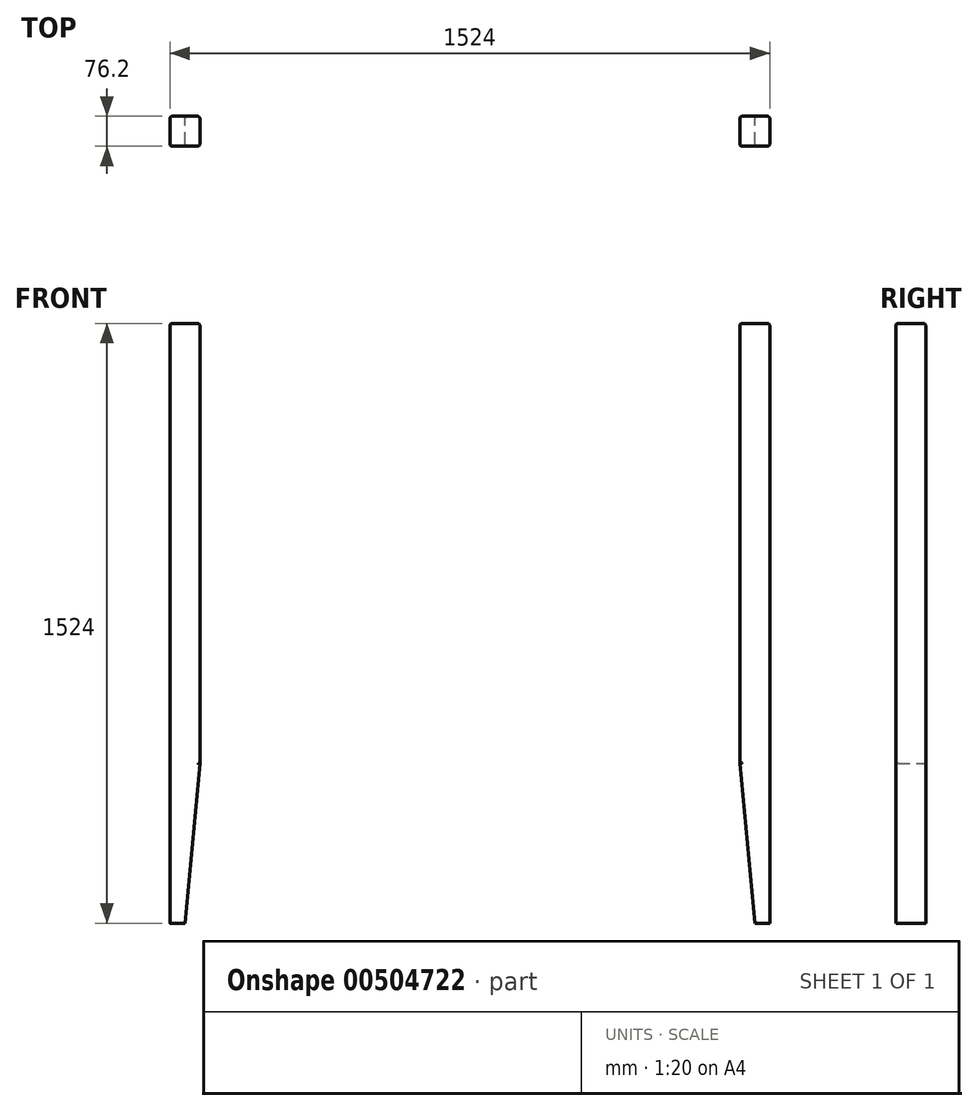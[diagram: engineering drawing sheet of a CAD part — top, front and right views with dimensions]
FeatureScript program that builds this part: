
annotation { "Feature Type Name" : "Feature", "Feature Type Description" : "" }
export const myFeature = defineFeature(function(context is Context, id is Id, definition is map)
    precondition{}
    {
        {
            var Q0;
            Q0=qCreatedBy(makeId("Front.planeOp"),FACE);
            var sketch = newSketch(context, id + "F0", { "sketchPlane" : qUnion([Q0])});
            skLineSegment(sketch, "E0", {"start": v(0, 0) * mm, "end": v(0, 1524) * mm});
            skLineSegment(sketch, "E1", {"start": v(0, 1524) * mm, "end": v(76.2, 1524) * mm});
            skLineSegment(sketch, "E2", {"start": v(76.2, 1524) * mm, "end": v(76.2, 406.4) * mm});
            skLineSegment(sketch, "E3", {"start": v(76.2, 406.4) * mm, "end": v(38.1, 0) * mm});
            skLineSegment(sketch, "E4", {"start": v(38.1, 0) * mm, "end": v(0, 0) * mm});
            skLineSegment(sketch, "E5", {"start": v(762, 1524) * mm, "end": v(762, 0) * mm, "construction": true});
            skLineSegment(sketch, "E6.MirrorCS", {"start": v(1524, 1524) * mm, "end": v(1447.8, 1524) * mm});
            skLineSegment(sketch, "E7.MirrorCS", {"start": v(1485.9, 0) * mm, "end": v(1524, 0) * mm});
            skLineSegment(sketch, "E8.MirrorCS", {"start": v(1524, 0) * mm, "end": v(1524, 1524) * mm});
            skLineSegment(sketch, "E9.MirrorCS", {"start": v(1447.8, 1524) * mm, "end": v(1447.8, 406.4) * mm});
            skLineSegment(sketch, "E10.MirrorCS", {"start": v(1447.8, 406.4) * mm, "end": v(1485.9, 0) * mm});
            skSolve(sketch);
        }
        {
            var Q0;
            Q0=makeQuery(id+"F0.imprint","IMPRINT",FACE,{"disambiguationData":[TD([[makeQuery(id+"F0.imprint","IMPRINT",EDGE,{"derivedFrom":sQuery(id+"F0.wireOp",EDGE,"E0")}),-1.0]])]});
            extrude(context, id + "F1", {"entities" : qUnion([Q0]), "depth" : 76.2 * mm});
        }
        {
            var Q0;
            Q0=makeQuery(id+"F0.imprint","IMPRINT",FACE,{"disambiguationData":[TD([[makeQuery(id+"F0.imprint","IMPRINT",EDGE,{"derivedFrom":sQuery(id+"F0.wireOp",EDGE,"E6.MirrorCS")}),1.0]])]});
            extrude(context, id + "F2", {"entities" : qUnion([Q0]), "depth" : 76.2 * mm});
        }
        {
            var Q0;
            Q0=makeQuery(id+"F1.opExtrude","CAP_EDGE",EDGE,{"disambiguationData":[OSD([sQuery(id+"F0.wireOp",EDGE,"E2")])],"isStart":false});
            var Q1;
            Q1=makeQuery(id+"F1.opExtrude","CAP_EDGE",EDGE,{"disambiguationData":[OSD([sQuery(id+"F0.wireOp",EDGE,"E3")])],"isStart":false});
            var Q2;
            Q2=makeQuery(id+"F1.opExtrude","CAP_EDGE",EDGE,{"disambiguationData":[OSD([sQuery(id+"F0.wireOp",EDGE,"E3")])],"isStart":true});
            var Q3;
            Q3=makeQuery(id+"F1.opExtrude","CAP_EDGE",EDGE,{"disambiguationData":[OSD([sQuery(id+"F0.wireOp",EDGE,"E2")])],"isStart":true});
            var Q4;
            Q4=makeQuery(id+"F1.opExtrude","CAP_EDGE",EDGE,{"disambiguationData":[OSD([sQuery(id+"F0.wireOp",EDGE,"E0")])],"isStart":false});
            var Q5;
            Q5=makeQuery(id+"F1.opExtrude","CAP_EDGE",EDGE,{"disambiguationData":[OSD([sQuery(id+"F0.wireOp",EDGE,"E0")])],"isStart":true});
            var Q6;
            Q6=makeQuery(id+"F2.opExtrude","CAP_EDGE",EDGE,{"disambiguationData":[OSD([sQuery(id+"F0.wireOp",EDGE,"E9.MirrorCS")])],"isStart":false});
            var Q7;
            Q7=makeQuery(id+"F2.opExtrude","CAP_EDGE",EDGE,{"disambiguationData":[OSD([sQuery(id+"F0.wireOp",EDGE,"E8.MirrorCS")])],"isStart":false});
            var Q8;
            Q8=makeQuery(id+"F2.opExtrude","CAP_EDGE",EDGE,{"disambiguationData":[OSD([sQuery(id+"F0.wireOp",EDGE,"E8.MirrorCS")])],"isStart":true});
            var Q9;
            Q9=makeQuery(id+"F2.opExtrude","CAP_EDGE",EDGE,{"disambiguationData":[OSD([sQuery(id+"F0.wireOp",EDGE,"E9.MirrorCS")])],"isStart":true});
            var Q10;
            Q10=makeQuery(id+"F2.opExtrude","CAP_EDGE",EDGE,{"disambiguationData":[OSD([sQuery(id+"F0.wireOp",EDGE,"E10.MirrorCS")])],"isStart":true});
            var Q11;
            Q11=makeQuery(id+"F2.opExtrude","CAP_EDGE",EDGE,{"disambiguationData":[OSD([sQuery(id+"F0.wireOp",EDGE,"E10.MirrorCS")])],"isStart":false});
            var Q12;
            Q12=makeQuery(id+"F2.opExtrude","CAP_EDGE",EDGE,{"disambiguationData":[OSD([sQuery(id+"F0.wireOp",EDGE,"E6.MirrorCS")])],"isStart":false});
            var Q13;
            Q13=makeQuery(id+"F2.opExtrude","SWEPT_EDGE",EDGE,{"disambiguationData":[OSD([sQuery(id+"F0.wireOp",EDGE,"E6.MirrorCS"),sQuery(id+"F0.wireOp",EDGE,"E8.MirrorCS")])]});
            var Q14;
            Q14=makeQuery(id+"F2.opExtrude","SWEPT_EDGE",EDGE,{"disambiguationData":[OSD([sQuery(id+"F0.wireOp",EDGE,"E6.MirrorCS"),sQuery(id+"F0.wireOp",EDGE,"E9.MirrorCS")])]});
            var Q15;
            Q15=makeQuery(id+"F2.opExtrude","CAP_EDGE",EDGE,{"disambiguationData":[OSD([sQuery(id+"F0.wireOp",EDGE,"E6.MirrorCS")])],"isStart":true});
            var Q16;
            Q16=makeQuery(id+"F1.opExtrude","SWEPT_EDGE",EDGE,{"disambiguationData":[OSD([sQuery(id+"F0.wireOp",EDGE,"E0"),sQuery(id+"F0.wireOp",EDGE,"E1")])]});
            var Q17;
            Q17=makeQuery(id+"F1.opExtrude","CAP_EDGE",EDGE,{"disambiguationData":[OSD([sQuery(id+"F0.wireOp",EDGE,"E1")])],"isStart":true});
            var Q18;
            Q18=makeQuery(id+"F1.opExtrude","SWEPT_EDGE",EDGE,{"disambiguationData":[OSD([sQuery(id+"F0.wireOp",EDGE,"E1"),sQuery(id+"F0.wireOp",EDGE,"E2")])]});
            var Q19;
            Q19=makeQuery(id+"F1.opExtrude","CAP_EDGE",EDGE,{"disambiguationData":[OSD([sQuery(id+"F0.wireOp",EDGE,"E1")])],"isStart":false});
            fillet(context, id + "F3", {"entities" : qUnion([Q0, Q1, Q2, Q3, Q4, Q5, Q6, Q7, Q8, Q9, Q10, Q11, Q12, Q13, Q14, Q15, Q16, Q17, Q18, Q19]), "radius" : 6.35 * mm, "tangentPropagation" : true, "allowEdgeOverflow" : false});
        }
    });
